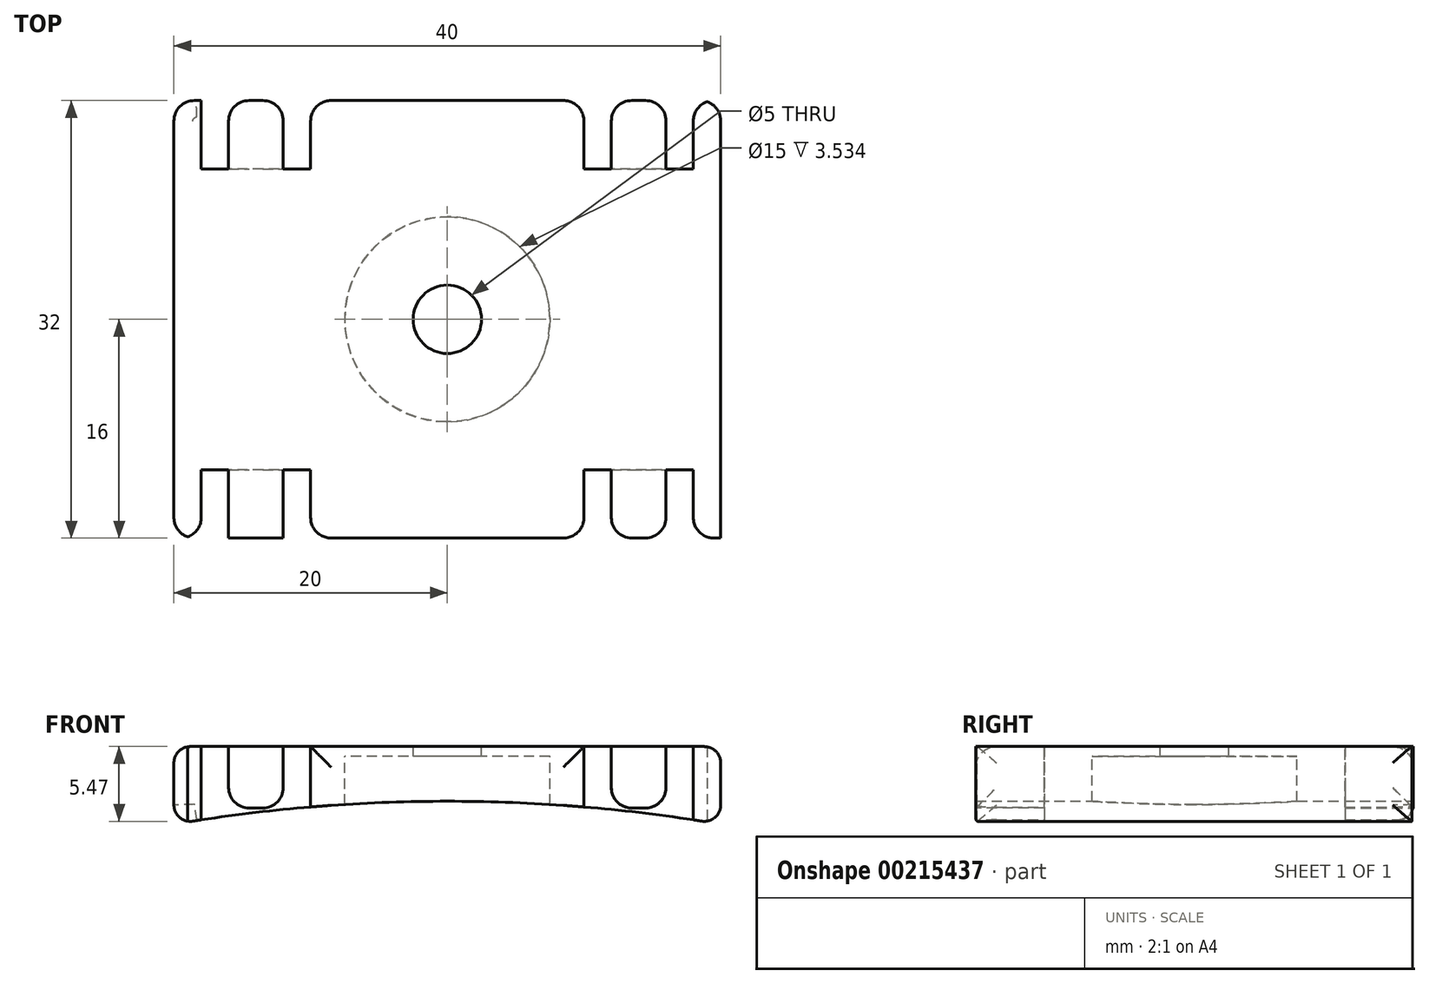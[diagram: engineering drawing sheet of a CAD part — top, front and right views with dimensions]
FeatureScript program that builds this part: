
annotation { "Feature Type Name" : "Feature", "Feature Type Description" : "" }
export const myFeature = defineFeature(function(context is Context, id is Id, definition is map)
    precondition{}
    {
        {
            var Q0;
            Q0=qCreatedBy(makeId("Front.planeOp"),FACE);
            var sketch = newSketch(context, id + "F0", { "sketchPlane" : qUnion([Q0])});
            skLineSegment(sketch, "E0", {"start": v(0, 0) * mm, "end": v(-20, 0) * mm});
            skLineSegment(sketch, "E1", {"start": v(-20, 0) * mm, "end": v(-20, -5.68) * mm});
            skLineSegment(sketch, "E2", {"start": v(0, 0) * mm, "end": v(0, -4) * mm});
            skArc(sketch, "E3", {"start": v(0, -4) * mm, "mid": v(-10.04, -4.42) * mm, "end": v(-20, -5.68) * mm});
            skSolve(sketch);
        }
        {
            var Q0;
            Q0 = qSketchRegion(id + "F0", true);
            extrude(context, id + "F1", {"entities" : qUnion([Q0]), "endBound" : BoundingType.SYMMETRIC, "depth" : 32 * mm});
        }
        {
            var Q0;
            Q0=makeQuery(id+"F1.opExtrude","SWEPT_BODY",BODY,{"disambiguationData":[OSD([sQuery(id+"F0.wireOp",EDGE,"E0"),sQuery(id+"F0.wireOp",EDGE,"E1"),sQuery(id+"F0.wireOp",EDGE,"E2"),sQuery(id+"F0.wireOp",EDGE,"E3")])]});
            var Q1;
            Q1=qCreatedBy(makeId("Right.planeOp"),FACE);
            mirror(context, id + "F2", {"operationType" : NewBodyOperationType.ADD, "entities" : qUnion([Q0]), "mirrorPlane" : qUnion([Q1])});
        }
        {
            var Q0;
            Q0=qCreatedBy(makeId("Top.planeOp"),FACE);
            var sketch = newSketch(context, id + "F3", { "sketchPlane" : qUnion([Q0])});
            skCircle(sketch, "E4", {"center": v(0, 0) * mm, "radius": 2.5 * mm});
            skSolve(sketch);
        }
        {
            var Q0;
            Q0 = qSketchRegion(id + "F3", true);
            extrude(context, id + "F4", {"entities" : qUnion([Q0]), "operationType" : NewBodyOperationType.REMOVE, "oppositeDirection" : true, "depth" : 5 * mm});
        }
        {
            var Q0;
            Q0=qCreatedBy(makeId("Top.planeOp"),FACE);
            cPlane(context, id + "F5", {"entities" : qUnion([Q0]), "cplaneType" : CPlaneType.OFFSET, "offset" : 4.2 * mm, "oppositeDirection" : true, "width" : 150 * mm, "height" : 150 * mm});
        }
        {
            var Q0;
            Q0=qCreatedBy(id+"F5.planeOp",FACE);
            var sketch = newSketch(context, id + "F6", { "sketchPlane" : qUnion([Q0])});
            skCircle(sketch, "E5", {"center": v(0, 0) * mm, "radius": 7.5 * mm});
            skSolve(sketch);
        }
        {
            var Q0;
            Q0 = qSketchRegion(id + "F6", true);
            extrude(context, id + "F7", {"entities" : qUnion([Q0]), "operationType" : NewBodyOperationType.REMOVE, "flatOperationType" : FlatOperationType.REMOVE, "endBound" : BoundingType.SYMMETRIC, "oppositeDirection" : true, "offsetDistance" : 25 * mm, "depth" : 7 * mm, "domain" : OperationDomain.MODEL});
        }
        {
            var Q0;
            Q0=qCreatedBy(makeId("Top.planeOp"),FACE);
            var sketch = newSketch(context, id + "F8", { "sketchPlane" : qUnion([Q0])});
            skCircle(sketch, "E6", {"center": v(0, 0) * mm, "radius": 15 * mm});
            skSolve(sketch);
        }
        {
            var Q0;
            Q0=qCreatedBy(makeId("Front.planeOp"),FACE);
            cPlane(context, id + "F9", {"entities" : qUnion([Q0]), "cplaneType" : CPlaneType.OFFSET, "offset" : 16 * mm, "width" : 150 * mm, "height" : 150 * mm});
        }
        {
            var Q0;
            Q0=qCreatedBy(id+"F9.planeOp",FACE);
            var sketch = newSketch(context, id + "F10", { "sketchPlane" : qUnion([Q0])});
            skLineSegment(sketch, "E7", {"start": v(-18, 0) * mm, "end": v(-18, -5.68) * mm});
            skLineSegment(sketch, "E8", {"start": v(-18, -5.68) * mm, "end": v(-10, -5.68) * mm});
            skLineSegment(sketch, "E9", {"start": v(-10, -5.68) * mm, "end": v(-10, 0) * mm});
            skLineSegment(sketch, "E10", {"start": v(-10, 0) * mm, "end": v(-12, 0) * mm});
            skLineSegment(sketch, "E11", {"start": v(-12, 0) * mm, "end": v(-12, -4.5) * mm});
            skLineSegment(sketch, "E12", {"start": v(-12, -4.5) * mm, "end": v(-16, -4.5) * mm});
            skLineSegment(sketch, "E13", {"start": v(-16, -4.5) * mm, "end": v(-16, 0) * mm});
            skLineSegment(sketch, "E14", {"start": v(-16, 0) * mm, "end": v(-18, 0) * mm});
            skLineSegment(sketch, "E15", {"start": v(18, 0) * mm, "end": v(18, -5.68) * mm});
            skLineSegment(sketch, "E16", {"start": v(18, -5.68) * mm, "end": v(10, -5.68) * mm});
            skLineSegment(sketch, "E17", {"start": v(10, -5.68) * mm, "end": v(10, 0) * mm});
            skLineSegment(sketch, "E18", {"start": v(10, 0) * mm, "end": v(12, 0) * mm});
            skLineSegment(sketch, "E19", {"start": v(12, 0) * mm, "end": v(12, -4.5) * mm});
            skLineSegment(sketch, "E20", {"start": v(12, -4.5) * mm, "end": v(16, -4.5) * mm});
            skLineSegment(sketch, "E21", {"start": v(16, -4.5) * mm, "end": v(16, 0) * mm});
            skLineSegment(sketch, "E22", {"start": v(16, 0) * mm, "end": v(18, 0) * mm});
            skSolve(sketch);
        }
        {
            var Q0;
            Q0 = qSketchRegion(id + "F10", true);
            extrude(context, id + "F11", {"entities" : qUnion([Q0]), "operationType" : NewBodyOperationType.REMOVE, "oppositeDirection" : true, "depth" : 5 * mm});
        }
        {
            var Q0;
            Q0=qCreatedBy(makeId("Front.planeOp"),FACE);
            cPlane(context, id + "F12", {"entities" : qUnion([Q0]), "cplaneType" : CPlaneType.OFFSET, "offset" : 16 * mm, "oppositeDirection" : true, "width" : 150 * mm, "height" : 150 * mm});
        }
        {
            var Q0;
            Q0=qCreatedBy(id+"F12.planeOp",FACE);
            var sketch = newSketch(context, id + "F13", { "sketchPlane" : qUnion([Q0])});
            skLineSegment(sketch, "E23", {"start": v(18, 0) * mm, "end": v(18, -5.63) * mm});
            skLineSegment(sketch, "E24", {"start": v(18, -5.63) * mm, "end": v(10, -5.63) * mm});
            skLineSegment(sketch, "E25", {"start": v(10, -5.63) * mm, "end": v(10, 0) * mm});
            skLineSegment(sketch, "E26", {"start": v(10, 0) * mm, "end": v(12, 0) * mm});
            skLineSegment(sketch, "E27", {"start": v(12, 0) * mm, "end": v(12, -4.5) * mm});
            skLineSegment(sketch, "E28", {"start": v(12, -4.5) * mm, "end": v(16, -4.5) * mm});
            skLineSegment(sketch, "E29", {"start": v(16, -4.5) * mm, "end": v(16, 0) * mm});
            skLineSegment(sketch, "E30", {"start": v(16, 0) * mm, "end": v(18, 0) * mm});
            skLineSegment(sketch, "E31", {"start": v(-18, 0) * mm, "end": v(-18, -5.68) * mm});
            skLineSegment(sketch, "E32", {"start": v(-18, -5.68) * mm, "end": v(-10, -5.68) * mm});
            skLineSegment(sketch, "E33", {"start": v(-10, -5.68) * mm, "end": v(-10, 0) * mm});
            skLineSegment(sketch, "E34", {"start": v(-10, 0) * mm, "end": v(-12, 0) * mm});
            skLineSegment(sketch, "E35", {"start": v(-12, 0) * mm, "end": v(-12, -4.5) * mm});
            skLineSegment(sketch, "E36", {"start": v(-12, -4.5) * mm, "end": v(-16, -4.5) * mm});
            skLineSegment(sketch, "E37", {"start": v(-16, -4.5) * mm, "end": v(-16, 0) * mm});
            skLineSegment(sketch, "E38", {"start": v(-16, 0) * mm, "end": v(-18, 0) * mm});
            skSolve(sketch);
        }
        {
            var Q0;
            Q0 = qSketchRegion(id + "F13", true);
            extrude(context, id + "F14", {"entities" : qUnion([Q0]), "operationType" : NewBodyOperationType.REMOVE, "depth" : 5 * mm});
        }
        {
            var Q0;
            Q0=makeQuery(id+"F11.boolean.opBoolean","COPY",EDGE,{"derivedFrom":makeQuery(id+"F11.opExtrude","CAP_EDGE",EDGE,{"disambiguationData":[OSD([sQuery(id+"F10.wireOp",EDGE,"E9")])],"isStart":true})});
            var Q1;
            Q1=makeQuery(id+"F11.boolean.opBoolean","COPY",EDGE,{"derivedFrom":makeQuery(id+"F11.opExtrude","CAP_EDGE",EDGE,{"disambiguationData":[OSD([sQuery(id+"F10.wireOp",EDGE,"E11")])],"isStart":true})});
            var Q2;
            Q2=makeQuery(id+"F11.boolean.opBoolean","COPY",EDGE,{"derivedFrom":makeQuery(id+"F11.opExtrude","CAP_EDGE",EDGE,{"disambiguationData":[OSD([sQuery(id+"F10.wireOp",EDGE,"E13")])],"isStart":true})});
            var Q3;
            Q3=makeQuery(id+"F11.boolean.opBoolean","COPY",EDGE,{"derivedFrom":makeQuery(id+"F11.opExtrude","CAP_EDGE",EDGE,{"disambiguationData":[OSD([sQuery(id+"F10.wireOp",EDGE,"E7")])],"isStart":true})});
            var Q4;
            Q4=makeQuery(id+"F1.opExtrude","CAP_EDGE",EDGE,{"disambiguationData":[OSD([sQuery(id+"F0.wireOp",EDGE,"E1")])],"isStart":false});
            var Q5;
            Q5=makeQuery(id+"F11.boolean.opBoolean","COPY",EDGE,{"derivedFrom":makeQuery(id+"F11.opExtrude","CAP_EDGE",EDGE,{"disambiguationData":[OSD([sQuery(id+"F10.wireOp",EDGE,"E19")])],"isStart":true})});
            var Q6;
            Q6=makeQuery(id+"F11.boolean.opBoolean","COPY",EDGE,{"derivedFrom":makeQuery(id+"F11.opExtrude","CAP_EDGE",EDGE,{"disambiguationData":[OSD([sQuery(id+"F10.wireOp",EDGE,"E17")])],"isStart":true})});
            var Q7;
            Q7=makeQuery(id+"F11.boolean.opBoolean","COPY",EDGE,{"derivedFrom":makeQuery(id+"F11.opExtrude","CAP_EDGE",EDGE,{"disambiguationData":[OSD([sQuery(id+"F10.wireOp",EDGE,"E21")])],"isStart":true})});
            var Q8;
            Q8=makeQuery(id+"F11.boolean.opBoolean","COPY",EDGE,{"derivedFrom":makeQuery(id+"F11.opExtrude","CAP_EDGE",EDGE,{"disambiguationData":[OSD([sQuery(id+"F10.wireOp",EDGE,"E15")])],"isStart":true})});
            var Q9;
            {var subQ0=sQuery(id+"F0.wireOp",EDGE,"E0");var subQ3=makeQuery(id+"F1.opExtrude","CAP_EDGE",EDGE,{"disambiguationData":[OSD([subQ0])],"isStart":false});Q9=makeQuery(id+"F11.boolean.opBoolean","SPLIT",EDGE,{"disambiguationData":[TD([makeQuery(id+"F11.opExtrude","SWEPT_FACE",FACE,{"disambiguationData":[OSD([sQuery(id+"F10.wireOp",EDGE,"E9")])]})])],"derivedFrom":makeQuery(id+"F2.boolean.opBoolean","MERGE",EDGE,{"derivedFrom":[subQ3,makeQuery(id+"F2.opPattern","COPY",EDGE,{"derivedFrom":subQ3,"instanceName":"1"})]})});}
            var Q10;
            {var subQ0=sQuery(id+"F0.wireOp",EDGE,"E3");var subQ3=makeQuery(id+"F1.opExtrude","CAP_EDGE",EDGE,{"disambiguationData":[OSD([subQ0])],"isStart":false});Q10=makeQuery(id+"F11.boolean.opBoolean","SPLIT",EDGE,{"disambiguationData":[TD([makeQuery(id+"F11.opExtrude","SWEPT_FACE",FACE,{"disambiguationData":[OSD([sQuery(id+"F10.wireOp",EDGE,"E9")])]})])],"derivedFrom":makeQuery(id+"F2.boolean.opBoolean","MERGE",EDGE,{"derivedFrom":[subQ3,makeQuery(id+"F2.opPattern","COPY",EDGE,{"derivedFrom":subQ3,"instanceName":"1"})]})});}
            var Q11;
            Q11=makeQuery(id+"F11.boolean.opBoolean","COPY",EDGE,{"derivedFrom":makeQuery(id+"F11.opExtrude","SWEPT_EDGE",EDGE,{"disambiguationData":[OSD([sQuery(id+"F10.wireOp",EDGE,"E9"),sQuery(id+"F10.wireOp",EDGE,"E10")])]})});
            var Q12;
            Q12=makeQuery(id+"F11.boolean.opBoolean","COPY",EDGE,{"derivedFrom":makeQuery(id+"F11.opExtrude","SWEPT_EDGE",EDGE,{"disambiguationData":[OSD([sQuery(id+"F10.wireOp",EDGE,"E10"),sQuery(id+"F10.wireOp",EDGE,"E11")])]})});
            var Q13;
            Q13=makeQuery(id+"F11.boolean.opBoolean","COPY",EDGE,{"derivedFrom":makeQuery(id+"F11.opExtrude","SWEPT_EDGE",EDGE,{"disambiguationData":[OSD([sQuery(id+"F10.wireOp",EDGE,"E13"),sQuery(id+"F10.wireOp",EDGE,"E14")])]})});
            var Q14;
            Q14=makeQuery(id+"F14.boolean.opBoolean","COPY",EDGE,{"derivedFrom":makeQuery(id+"F14.opExtrude","SWEPT_EDGE",EDGE,{"disambiguationData":[OSD([sQuery(id+"F13.wireOp",EDGE,"E37"),sQuery(id+"F13.wireOp",EDGE,"E38")])]})});
            var Q15;
            Q15=makeQuery(id+"F14.boolean.opBoolean","COPY",EDGE,{"derivedFrom":makeQuery(id+"F14.opExtrude","SWEPT_EDGE",EDGE,{"disambiguationData":[OSD([sQuery(id+"F13.wireOp",EDGE,"E34"),sQuery(id+"F13.wireOp",EDGE,"E35")])]})});
            var Q16;
            Q16=makeQuery(id+"F14.boolean.opBoolean","COPY",EDGE,{"derivedFrom":makeQuery(id+"F14.opExtrude","SWEPT_EDGE",EDGE,{"disambiguationData":[OSD([sQuery(id+"F13.wireOp",EDGE,"E25"),sQuery(id+"F13.wireOp",EDGE,"E26")])]})});
            var Q17;
            Q17=makeQuery(id+"F14.boolean.opBoolean","COPY",EDGE,{"derivedFrom":makeQuery(id+"F14.opExtrude","SWEPT_EDGE",EDGE,{"disambiguationData":[OSD([sQuery(id+"F13.wireOp",EDGE,"E26"),sQuery(id+"F13.wireOp",EDGE,"E27")])]})});
            var Q18;
            Q18=makeQuery(id+"F14.boolean.opBoolean","COPY",EDGE,{"derivedFrom":makeQuery(id+"F14.opExtrude","SWEPT_EDGE",EDGE,{"disambiguationData":[OSD([sQuery(id+"F13.wireOp",EDGE,"E29"),sQuery(id+"F13.wireOp",EDGE,"E30")])]})});
            var Q19;
            Q19=makeQuery(id+"F1.opExtrude","CAP_EDGE",EDGE,{"disambiguationData":[OSD([sQuery(id+"F0.wireOp",EDGE,"E1")])],"isStart":true});
            var Q20;
            Q20=makeQuery(id+"F14.boolean.opBoolean","COPY",EDGE,{"derivedFrom":makeQuery(id+"F14.opExtrude","CAP_EDGE",EDGE,{"disambiguationData":[OSD([sQuery(id+"F13.wireOp",EDGE,"E31")])],"isStart":true})});
            var Q21;
            Q21=makeQuery(id+"F14.boolean.opBoolean","COPY",EDGE,{"derivedFrom":makeQuery(id+"F14.opExtrude","CAP_EDGE",EDGE,{"disambiguationData":[OSD([sQuery(id+"F13.wireOp",EDGE,"E37")])],"isStart":true})});
            var Q22;
            Q22=makeQuery(id+"F14.boolean.opBoolean","COPY",EDGE,{"derivedFrom":makeQuery(id+"F14.opExtrude","CAP_EDGE",EDGE,{"disambiguationData":[OSD([sQuery(id+"F13.wireOp",EDGE,"E35")])],"isStart":true})});
            var Q23;
            Q23=makeQuery(id+"F14.boolean.opBoolean","COPY",EDGE,{"derivedFrom":makeQuery(id+"F14.opExtrude","CAP_EDGE",EDGE,{"disambiguationData":[OSD([sQuery(id+"F13.wireOp",EDGE,"E33")])],"isStart":true})});
            var Q24;
            Q24=makeQuery(id+"F14.boolean.opBoolean","COPY",EDGE,{"derivedFrom":makeQuery(id+"F14.opExtrude","SWEPT_EDGE",EDGE,{"disambiguationData":[OSD([sQuery(id+"F13.wireOp",EDGE,"E33"),sQuery(id+"F13.wireOp",EDGE,"E34")])]})});
            var Q25;
            Q25=makeQuery(id+"F14.boolean.opBoolean","COPY",EDGE,{"derivedFrom":makeQuery(id+"F14.opExtrude","CAP_EDGE",EDGE,{"disambiguationData":[OSD([sQuery(id+"F13.wireOp",EDGE,"E25")])],"isStart":true})});
            var Q26;
            Q26=makeQuery(id+"F14.boolean.opBoolean","COPY",EDGE,{"derivedFrom":makeQuery(id+"F14.opExtrude","CAP_EDGE",EDGE,{"disambiguationData":[OSD([sQuery(id+"F13.wireOp",EDGE,"E27")])],"isStart":true})});
            var Q27;
            Q27=makeQuery(id+"F14.boolean.opBoolean","COPY",EDGE,{"derivedFrom":makeQuery(id+"F14.opExtrude","CAP_EDGE",EDGE,{"disambiguationData":[OSD([sQuery(id+"F13.wireOp",EDGE,"E29")])],"isStart":true})});
            var Q28;
            Q28=makeQuery(id+"F14.boolean.opBoolean","COPY",EDGE,{"derivedFrom":makeQuery(id+"F14.opExtrude","CAP_EDGE",EDGE,{"disambiguationData":[OSD([sQuery(id+"F13.wireOp",EDGE,"E23")])],"isStart":true})});
            var Q29;
            Q29=makeQuery(id+"F2.opPattern","COPY",EDGE,{"derivedFrom":makeQuery(id+"F1.opExtrude","CAP_EDGE",EDGE,{"disambiguationData":[OSD([sQuery(id+"F0.wireOp",EDGE,"E1")])],"isStart":true}),"instanceName":"1"});
            var Q30;
            {var subQ0=sQuery(id+"F0.wireOp",EDGE,"E0");var subQ3=makeQuery(id+"F1.opExtrude","CAP_EDGE",EDGE,{"disambiguationData":[OSD([subQ0])],"isStart":true});Q30=makeQuery(id+"F14.boolean.opBoolean","SPLIT",EDGE,{"disambiguationData":[TD([makeQuery(id+"F14.opExtrude","SWEPT_FACE",FACE,{"disambiguationData":[OSD([sQuery(id+"F13.wireOp",EDGE,"E25")])]})])],"derivedFrom":makeQuery(id+"F2.boolean.opBoolean","MERGE",EDGE,{"derivedFrom":[subQ3,makeQuery(id+"F2.opPattern","COPY",EDGE,{"derivedFrom":subQ3,"instanceName":"1"})]})});}
            var Q31;
            {var subQ0=sQuery(id+"F0.wireOp",EDGE,"E3");var subQ3=makeQuery(id+"F1.opExtrude","CAP_EDGE",EDGE,{"disambiguationData":[OSD([subQ0])],"isStart":true});Q31=makeQuery(id+"F14.boolean.opBoolean","SPLIT",EDGE,{"disambiguationData":[TD([makeQuery(id+"F14.opExtrude","SWEPT_FACE",FACE,{"disambiguationData":[OSD([sQuery(id+"F13.wireOp",EDGE,"E25")])]})])],"derivedFrom":makeQuery(id+"F2.boolean.opBoolean","MERGE",EDGE,{"derivedFrom":[subQ3,makeQuery(id+"F2.opPattern","COPY",EDGE,{"derivedFrom":subQ3,"instanceName":"1"})]})});}
            var Q32;
            Q32=makeQuery(id+"F14.boolean.opBoolean","COPY",EDGE,{"derivedFrom":makeQuery(id+"F14.opExtrude","CAP_EDGE",EDGE,{"disambiguationData":[OSD([sQuery(id+"F13.wireOp",EDGE,"E26")])],"isStart":false})});
            var Q33;
            Q33=makeQuery(id+"F14.boolean.opBoolean","COPY",EDGE,{"derivedFrom":makeQuery(id+"F14.opExtrude","CAP_EDGE",EDGE,{"disambiguationData":[OSD([sQuery(id+"F13.wireOp",EDGE,"E30")])],"isStart":false})});
            var Q34;
            Q34=makeQuery(id+"F11.boolean.opBoolean","COPY",EDGE,{"derivedFrom":makeQuery(id+"F11.opExtrude","CAP_EDGE",EDGE,{"disambiguationData":[OSD([sQuery(id+"F10.wireOp",EDGE,"E18")])],"isStart":false})});
            var Q35;
            Q35=makeQuery(id+"F11.boolean.opBoolean","COPY",EDGE,{"derivedFrom":makeQuery(id+"F11.opExtrude","CAP_EDGE",EDGE,{"disambiguationData":[OSD([sQuery(id+"F10.wireOp",EDGE,"E22")])],"isStart":false})});
            var Q36;
            Q36=makeQuery(id+"F11.boolean.opBoolean","COPY",EDGE,{"derivedFrom":makeQuery(id+"F11.opExtrude","CAP_EDGE",EDGE,{"disambiguationData":[OSD([sQuery(id+"F10.wireOp",EDGE,"E14")])],"isStart":false})});
            var Q37;
            Q37=makeQuery(id+"F11.boolean.opBoolean","COPY",EDGE,{"derivedFrom":makeQuery(id+"F11.opExtrude","CAP_EDGE",EDGE,{"disambiguationData":[OSD([sQuery(id+"F10.wireOp",EDGE,"E10")])],"isStart":false})});
            var Q38;
            Q38=makeQuery(id+"F14.boolean.opBoolean","COPY",EDGE,{"derivedFrom":makeQuery(id+"F14.opExtrude","CAP_EDGE",EDGE,{"disambiguationData":[OSD([sQuery(id+"F13.wireOp",EDGE,"E38")])],"isStart":false})});
            var Q39;
            Q39=makeQuery(id+"F14.boolean.opBoolean","COPY",EDGE,{"derivedFrom":makeQuery(id+"F14.opExtrude","CAP_EDGE",EDGE,{"disambiguationData":[OSD([sQuery(id+"F13.wireOp",EDGE,"E34")])],"isStart":false})});
            var Q40;
            {var subQ0=makeQuery(id+"F1.opExtrude","SWEPT_FACE",FACE,{"disambiguationData":[OSD([sQuery(id+"F0.wireOp",EDGE,"E3")])]});Q40=makeQuery(id+"F14.boolean.opBoolean","INTERSECT",EDGE,{"derivedFrom":[makeQuery(id+"F2.boolean.opBoolean","MERGE",FACE,{"derivedFrom":[subQ0,makeQuery(id+"F2.opPattern","COPY",FACE,{"derivedFrom":subQ0,"instanceName":"1"})]}),makeQuery(id+"F14.opExtrude","SWEPT_FACE",FACE,{"disambiguationData":[OSD([sQuery(id+"F13.wireOp",EDGE,"E25")])]})]});}
            var Q41;
            {var subQ0=makeQuery(id+"F1.opExtrude","SWEPT_FACE",FACE,{"disambiguationData":[OSD([sQuery(id+"F0.wireOp",EDGE,"E3")])]});Q41=makeQuery(id+"F14.boolean.opBoolean","INTERSECT",EDGE,{"derivedFrom":[makeQuery(id+"F2.boolean.opBoolean","MERGE",FACE,{"derivedFrom":[subQ0,makeQuery(id+"F2.opPattern","COPY",FACE,{"derivedFrom":subQ0,"instanceName":"1"})]}),makeQuery(id+"F14.opExtrude","SWEPT_FACE",FACE,{"disambiguationData":[OSD([sQuery(id+"F13.wireOp",EDGE,"E33")])]})]});}
            var Q42;
            {var subQ0=makeQuery(id+"F1.opExtrude","SWEPT_FACE",FACE,{"disambiguationData":[OSD([sQuery(id+"F0.wireOp",EDGE,"E3")])]});Q42=makeQuery(id+"F11.boolean.opBoolean","INTERSECT",EDGE,{"derivedFrom":[makeQuery(id+"F2.boolean.opBoolean","MERGE",FACE,{"derivedFrom":[subQ0,makeQuery(id+"F2.opPattern","COPY",FACE,{"derivedFrom":subQ0,"instanceName":"1"})]}),makeQuery(id+"F11.opExtrude","SWEPT_FACE",FACE,{"disambiguationData":[OSD([sQuery(id+"F10.wireOp",EDGE,"E9")])]})]});}
            var Q43;
            {var subQ0=makeQuery(id+"F1.opExtrude","SWEPT_FACE",FACE,{"disambiguationData":[OSD([sQuery(id+"F0.wireOp",EDGE,"E3")])]});Q43=makeQuery(id+"F11.boolean.opBoolean","INTERSECT",EDGE,{"derivedFrom":[makeQuery(id+"F2.boolean.opBoolean","MERGE",FACE,{"derivedFrom":[subQ0,makeQuery(id+"F2.opPattern","COPY",FACE,{"derivedFrom":subQ0,"instanceName":"1"})]}),makeQuery(id+"F11.opExtrude","SWEPT_FACE",FACE,{"disambiguationData":[OSD([sQuery(id+"F10.wireOp",EDGE,"E17")])]})]});}
            var Q44;
            Q44=makeQuery(id+"F14.boolean.opBoolean","COPY",EDGE,{"derivedFrom":makeQuery(id+"F14.opExtrude","SWEPT_EDGE",EDGE,{"disambiguationData":[OSD([sQuery(id+"F13.wireOp",EDGE,"E28"),sQuery(id+"F13.wireOp",EDGE,"E29")])]})});
            var Q45;
            Q45=makeQuery(id+"F14.boolean.opBoolean","COPY",EDGE,{"derivedFrom":makeQuery(id+"F14.opExtrude","SWEPT_EDGE",EDGE,{"disambiguationData":[OSD([sQuery(id+"F13.wireOp",EDGE,"E27"),sQuery(id+"F13.wireOp",EDGE,"E28")])]})});
            var Q46;
            Q46=makeQuery(id+"F14.boolean.opBoolean","COPY",EDGE,{"derivedFrom":makeQuery(id+"F14.opExtrude","SWEPT_EDGE",EDGE,{"disambiguationData":[OSD([sQuery(id+"F13.wireOp",EDGE,"E35"),sQuery(id+"F13.wireOp",EDGE,"E36")])]})});
            var Q47;
            Q47=makeQuery(id+"F14.boolean.opBoolean","COPY",EDGE,{"derivedFrom":makeQuery(id+"F14.opExtrude","SWEPT_EDGE",EDGE,{"disambiguationData":[OSD([sQuery(id+"F13.wireOp",EDGE,"E36"),sQuery(id+"F13.wireOp",EDGE,"E37")])]})});
            var Q48;
            {var subQ0=makeQuery(id+"F1.opExtrude","SWEPT_FACE",FACE,{"disambiguationData":[OSD([sQuery(id+"F0.wireOp",EDGE,"E3")])]});Q48=makeQuery(id+"F14.boolean.opBoolean","INTERSECT",EDGE,{"derivedFrom":[makeQuery(id+"F2.boolean.opBoolean","MERGE",FACE,{"derivedFrom":[subQ0,makeQuery(id+"F2.opPattern","COPY",FACE,{"derivedFrom":subQ0,"instanceName":"1"})]}),makeQuery(id+"F14.opExtrude","SWEPT_FACE",FACE,{"disambiguationData":[OSD([sQuery(id+"F13.wireOp",EDGE,"E31")])]})]});}
            var Q49;
            {var subQ0=makeQuery(id+"F1.opExtrude","SWEPT_FACE",FACE,{"disambiguationData":[OSD([sQuery(id+"F0.wireOp",EDGE,"E3")])]});Q49=makeQuery(id+"F11.boolean.opBoolean","INTERSECT",EDGE,{"derivedFrom":[makeQuery(id+"F2.boolean.opBoolean","MERGE",FACE,{"derivedFrom":[subQ0,makeQuery(id+"F2.opPattern","COPY",FACE,{"derivedFrom":subQ0,"instanceName":"1"})]}),makeQuery(id+"F11.opExtrude","SWEPT_FACE",FACE,{"disambiguationData":[OSD([sQuery(id+"F10.wireOp",EDGE,"E7")])]})]});}
            var Q50;
            Q50=makeQuery(id+"F11.boolean.opBoolean","COPY",EDGE,{"derivedFrom":makeQuery(id+"F11.opExtrude","SWEPT_EDGE",EDGE,{"disambiguationData":[OSD([sQuery(id+"F10.wireOp",EDGE,"E12"),sQuery(id+"F10.wireOp",EDGE,"E13")])]})});
            var Q51;
            Q51=makeQuery(id+"F11.boolean.opBoolean","COPY",EDGE,{"derivedFrom":makeQuery(id+"F11.opExtrude","SWEPT_EDGE",EDGE,{"disambiguationData":[OSD([sQuery(id+"F10.wireOp",EDGE,"E11"),sQuery(id+"F10.wireOp",EDGE,"E12")])]})});
            var Q52;
            Q52=makeQuery(id+"F11.boolean.opBoolean","COPY",EDGE,{"derivedFrom":makeQuery(id+"F11.opExtrude","SWEPT_EDGE",EDGE,{"disambiguationData":[OSD([sQuery(id+"F10.wireOp",EDGE,"E19"),sQuery(id+"F10.wireOp",EDGE,"E20")])]})});
            var Q53;
            Q53=makeQuery(id+"F11.boolean.opBoolean","COPY",EDGE,{"derivedFrom":makeQuery(id+"F11.opExtrude","SWEPT_EDGE",EDGE,{"disambiguationData":[OSD([sQuery(id+"F10.wireOp",EDGE,"E20"),sQuery(id+"F10.wireOp",EDGE,"E21")])]})});
            var Q54;
            {var subQ0=makeQuery(id+"F1.opExtrude","SWEPT_FACE",FACE,{"disambiguationData":[OSD([sQuery(id+"F0.wireOp",EDGE,"E3")])]});Q54=makeQuery(id+"F11.boolean.opBoolean","INTERSECT",EDGE,{"derivedFrom":[makeQuery(id+"F2.boolean.opBoolean","MERGE",FACE,{"derivedFrom":[subQ0,makeQuery(id+"F2.opPattern","COPY",FACE,{"derivedFrom":subQ0,"instanceName":"1"})]}),makeQuery(id+"F11.opExtrude","SWEPT_FACE",FACE,{"disambiguationData":[OSD([sQuery(id+"F10.wireOp",EDGE,"E15")])]})]});}
            fillet(context, id + "F15", {"entities" : qUnion([Q0, Q1, Q2, Q3, Q4, Q5, Q6, Q7, Q8, Q9, Q10, Q11, Q12, Q13, Q14, Q15, Q16, Q17, Q18, Q19, Q20, Q21, Q22, Q23, Q24, Q25, Q26, Q27, Q28, Q29, Q30, Q31, Q32, Q33, Q34, Q35, Q36, Q37, Q38, Q39, Q40, Q41, Q42, Q43, Q44, Q45, Q46, Q47, Q48, Q49, Q50, Q51, Q52, Q53, Q54]), "radius" : 1.5 * mm, "tangentPropagation" : true, "defaultsChanged" : false, "vertexSettings" : [], "allowEdgeOverflow" : false});
        }
        {
            var Q0;
            Q0=makeQuery(id+"F1.opExtrude","SWEPT_EDGE",EDGE,{"disambiguationData":[OSD([sQuery(id+"F0.wireOp",EDGE,"E0"),sQuery(id+"F0.wireOp",EDGE,"E1")])]});
            var Q1;
            Q1=makeQuery(id+"F1.opExtrude","SWEPT_EDGE",EDGE,{"disambiguationData":[OSD([sQuery(id+"F0.wireOp",EDGE,"E1"),sQuery(id+"F0.wireOp",EDGE,"E3")])]});
            var Q2;
            Q2=makeQuery(id+"F2.opPattern","COPY",EDGE,{"derivedFrom":makeQuery(id+"F1.opExtrude","SWEPT_EDGE",EDGE,{"disambiguationData":[OSD([sQuery(id+"F0.wireOp",EDGE,"E0"),sQuery(id+"F0.wireOp",EDGE,"E1")])]}),"instanceName":"1"});
            var Q3;
            Q3=makeQuery(id+"F2.opPattern","COPY",EDGE,{"derivedFrom":makeQuery(id+"F1.opExtrude","SWEPT_EDGE",EDGE,{"disambiguationData":[OSD([sQuery(id+"F0.wireOp",EDGE,"E1"),sQuery(id+"F0.wireOp",EDGE,"E3")])]}),"instanceName":"1"});
            fillet(context, id + "F16", {"entities" : qUnion([Q0, Q1, Q2, Q3]), "radius" : 1.2 * mm, "tangentPropagation" : true, "allowEdgeOverflow" : false});
        }
    });
